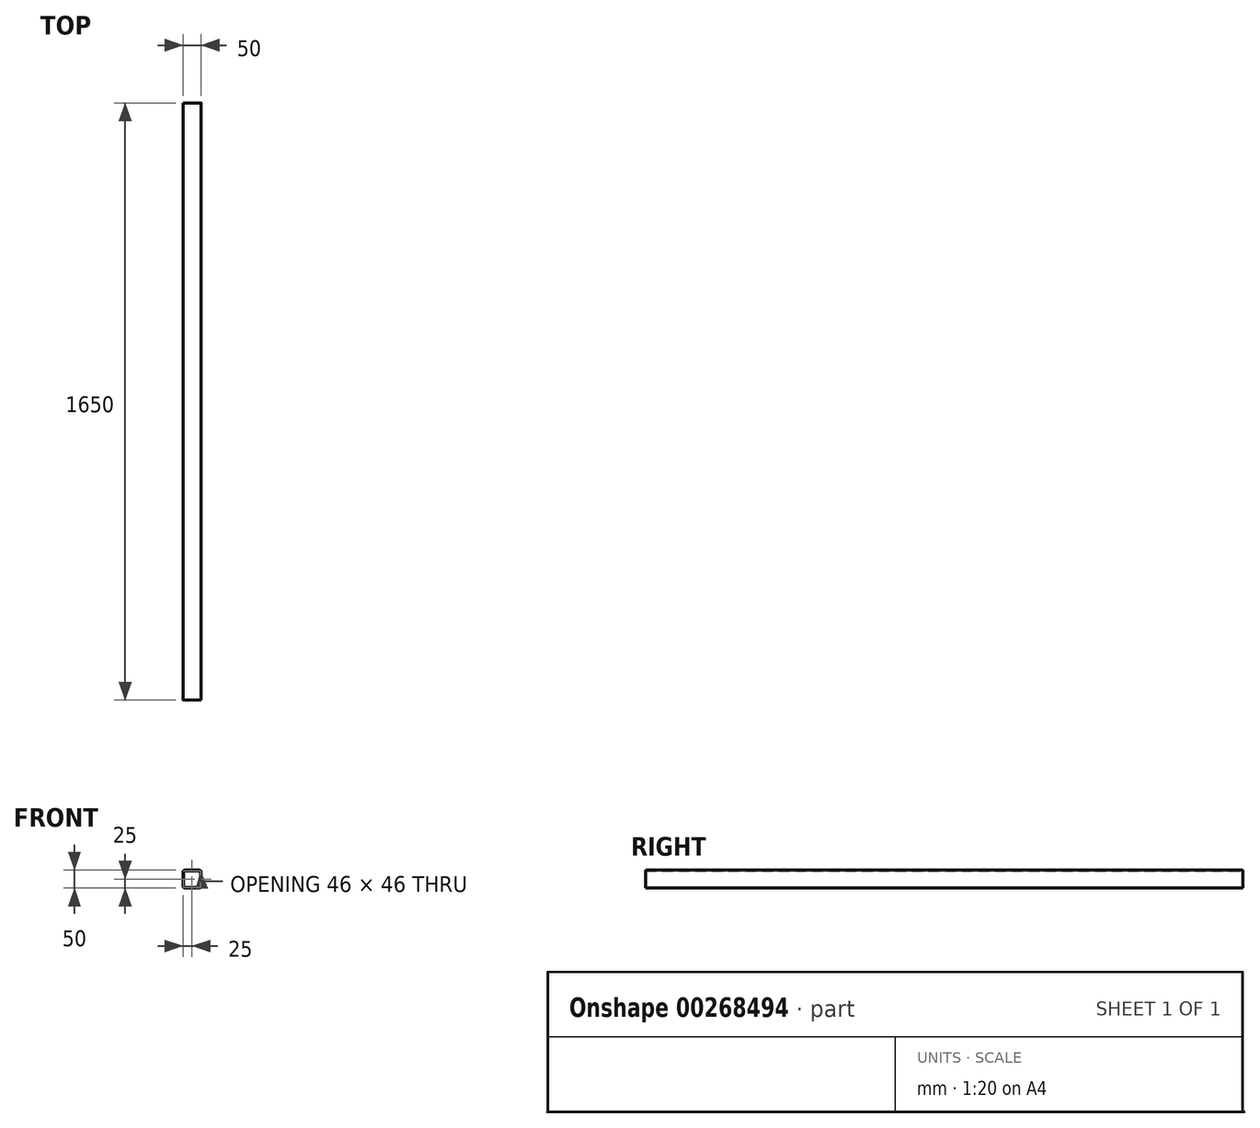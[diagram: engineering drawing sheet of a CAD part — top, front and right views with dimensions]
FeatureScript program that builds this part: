
annotation { "Feature Type Name" : "Feature", "Feature Type Description" : "" }
export const myFeature = defineFeature(function(context is Context, id is Id, definition is map)
    precondition{}
    {
        {
            var Q0;
            Q0=qCreatedBy(makeId("Front.planeOp"),FACE);
            var sketch = newSketch(context, id + "F0", { "sketchPlane" : qUnion([Q0])});
            skLineSegment(sketch, "E0", {"start": v(0, 23) * mm, "end": v(-20, 23) * mm});
            skLineSegment(sketch, "E1", {"start": v(-23, 20) * mm, "end": v(-23, -20) * mm});
            skLineSegment(sketch, "E2", {"start": v(-20, -23) * mm, "end": v(0, -23) * mm});
            skLineSegment(sketch, "E3", {"start": v(0, 25) * mm, "end": v(-19, 25) * mm});
            skLineSegment(sketch, "E4", {"start": v(-25, 19) * mm, "end": v(-25, -19) * mm});
            skLineSegment(sketch, "E5", {"start": v(-19, -25) * mm, "end": v(0, -25) * mm});
            skPoint(sketch, "E6.visualSharp", {"position": v(-23, 23) * mm});
            skArc(sketch, "E6.filletArc", {"start": v(-20, 23) * mm, "mid": v(-22.12, 22.12) * mm, "end": v(-23, 20) * mm});
            skPoint(sketch, "E7.visualSharp", {"position": v(-23, -23) * mm});
            skArc(sketch, "E7.filletArc", {"start": v(-23, -20) * mm, "mid": v(-22.12, -22.12) * mm, "end": v(-20, -23) * mm});
            skPoint(sketch, "E8.visualSharp", {"position": v(-25, 25) * mm});
            skArc(sketch, "E8.filletArc", {"start": v(-19, 25) * mm, "mid": v(-23.24, 23.24) * mm, "end": v(-25, 19) * mm});
            skPoint(sketch, "E9.visualSharp", {"position": v(-25, -25) * mm});
            skArc(sketch, "E9.filletArc", {"start": v(-25, -19) * mm, "mid": v(-23.24, -23.24) * mm, "end": v(-19, -25) * mm});
            skArc(sketch, "E10.MirrorCS", {"start": v(20, 23) * mm, "mid": v(22.12, 22.12) * mm, "end": v(23, 20) * mm});
            skArc(sketch, "E11.MirrorCS", {"start": v(23, -20) * mm, "mid": v(22.12, -22.12) * mm, "end": v(20, -23) * mm});
            skArc(sketch, "E12.MirrorCS", {"start": v(19, 25) * mm, "mid": v(23.24, 23.24) * mm, "end": v(25, 19) * mm});
            skArc(sketch, "E13.MirrorCS", {"start": v(25, -19) * mm, "mid": v(23.24, -23.24) * mm, "end": v(19, -25) * mm});
            skPoint(sketch, "E14.MirrorP", {"position": v(25, 25) * mm});
            skPoint(sketch, "E15.MirrorP", {"position": v(25, -25) * mm});
            skLineSegment(sketch, "E16.MirrorCS", {"start": v(0, 23) * mm, "end": v(20, 23) * mm});
            skPoint(sketch, "E17.MirrorP", {"position": v(23, -23) * mm});
            skLineSegment(sketch, "E18.MirrorCS", {"start": v(23, 20) * mm, "end": v(23, -20) * mm});
            skLineSegment(sketch, "E19.MirrorCS", {"start": v(20, -23) * mm, "end": v(0, -23) * mm});
            skPoint(sketch, "E20.MirrorP", {"position": v(23, 23) * mm});
            skLineSegment(sketch, "E21.MirrorCS", {"start": v(19, -25) * mm, "end": v(0, -25) * mm});
            skLineSegment(sketch, "E22.MirrorCS", {"start": v(0, 25) * mm, "end": v(19, 25) * mm});
            skLineSegment(sketch, "E23.MirrorCS", {"start": v(25, 19) * mm, "end": v(25, -19) * mm});
            skSolve(sketch);
        }
        {
            var Q0;
            Q0=qSketchRegion(id+"F0",true);
            extrude(context, id + "F1", {"entities" : qUnion([Q0]), "depth" : 1650 * mm});
        }
    });
